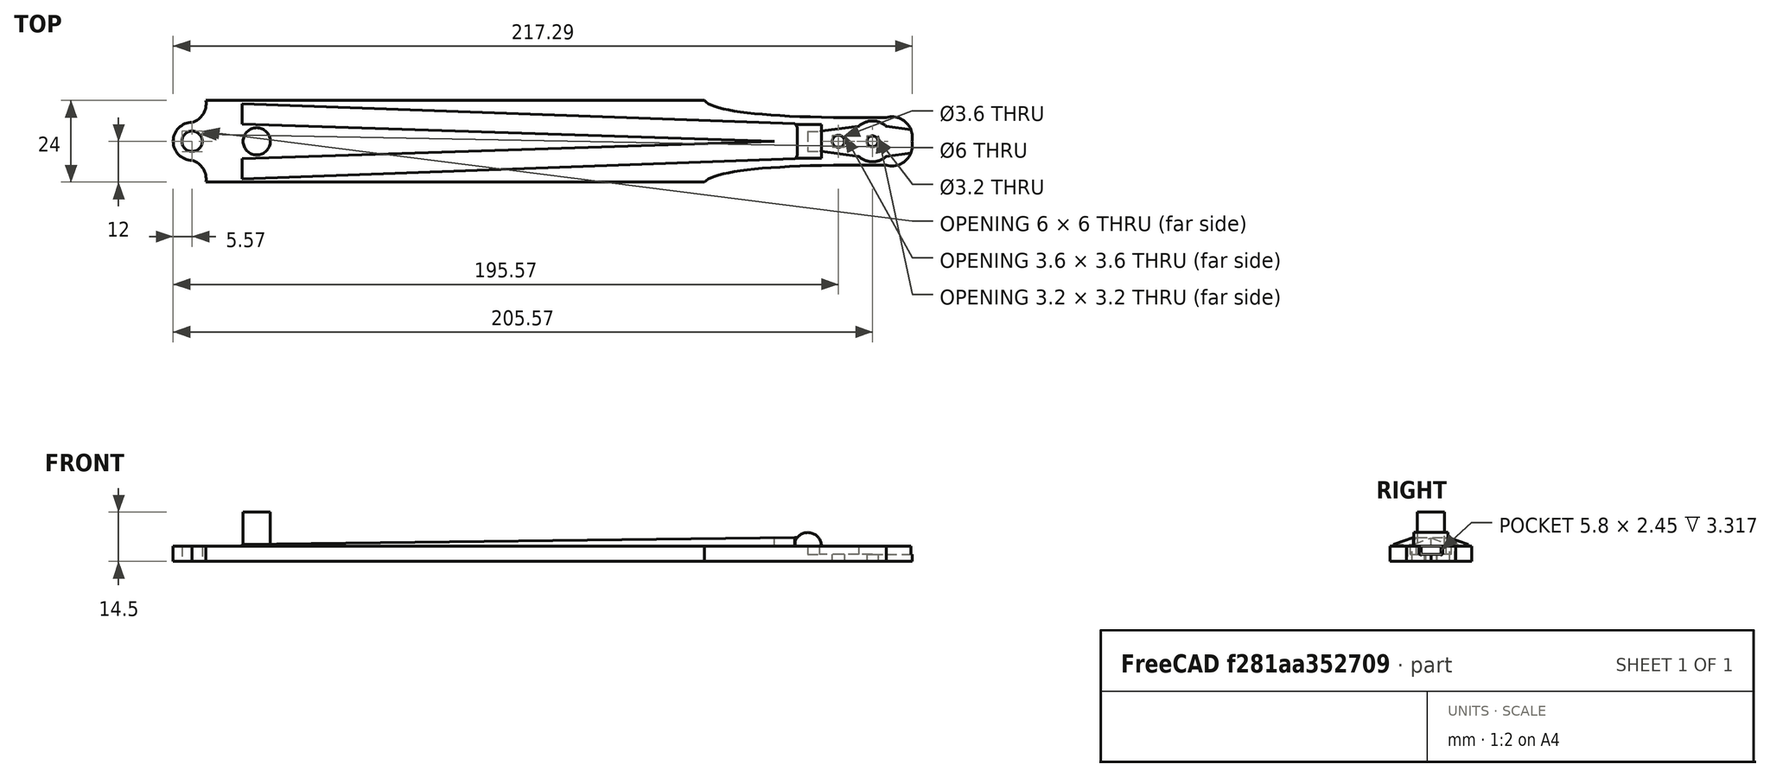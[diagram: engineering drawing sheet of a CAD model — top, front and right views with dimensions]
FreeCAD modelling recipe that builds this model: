
FCSTD DOCUMENT  (FreeCAD 0.18.4R)
Label: Servo_reset_Arm
License: All rights reserved
LicenseURL: http://en.wikipedia.org/wiki/All_rights_reserved
objects: TechDraw::DrawViewDimension×10, Sketcher::SketchObject×8, TechDraw::DrawViewPart×5, Part::Extrusion×4, Part::Mirroring×2, Part::MultiFuse×2, Part::Cut×2, TechDraw::DrawSVGTemplate×2, TechDraw::DrawViewAnnotation×2, TechDraw::DrawPage×2, PartDesign::Pad×2, Spreadsheet::Sheet×1, Part::Fuse×1, PartDesign::FeatureBase×1, PartDesign::Pocket×1, PartDesign::Body×1, TechDraw::DrawProjGroupItem×1, TechDraw::DrawProjGroup×1
note: 27 computed .brp shape members not serialized (recipe doc carries the construction recipe); baked Part::Feature solids carry a one-line shape summary decoded from their .brp

FEATURE [Sketcher::SketchObject] Sketch001
  sketch-geometry (19):
    g0: GeomPoint X=-195.949 Y=12 Z=0
    g1: LineSegment StartX=-195.949 StartY=12 StartZ=0 EndX=-49.4478 EndY=12 EndZ=0
    g2: Circle [constr] CenterX=4.05129 CenterY=7 CenterZ=0 NormalX=0 NormalY=0 NormalZ=1 AngleXU=0 Radius=6
    g3: ArcOfCircle CenterX=5.68089 CenterY=1.18713 CenterZ=0 NormalX=0 NormalY=0 NormalZ=1 AngleXU=0 Radius=6.03698 StartAngle=6.08525 EndAngle=8.12731
    g4: ArcOfCircle CenterX=0 CenterY=0 CenterZ=0 NormalX=0 NormalY=0 NormalZ=1 AngleXU=0 Radius=1.6 StartAngle=0 EndAngle=3.14159
    g5: LineSegment StartX=1.6 StartY=0 StartZ=0 EndX=11.6 EndY=0 EndZ=0
    g6: LineSegment StartX=-1.6 StartY=0 StartZ=0 EndX=-90.499 EndY=0 EndZ=0
    g7: Circle [constr] CenterX=4.05129 CenterY=7 CenterZ=0 NormalX=0 NormalY=0 NormalZ=1 AngleXU=0 Radius=5
    g8: Circle [constr] CenterX=-44.341 CenterY=6.58855 CenterZ=0 NormalX=0 NormalY=0 NormalZ=1 AngleXU=0 Radius=5
    g9: Circle [constr] CenterX=-49.4478 CenterY=12 CenterZ=0 NormalX=0 NormalY=0 NormalZ=1 AngleXU=0 Radius=5
    g10: BSplineCurve PolesCount=3 KnotsCount=2 Degree=2 IsPeriodic=0
    g11: GeomPoint [constr] X=4.05129 Y=7 Z=0
    g12: GeomPoint [constr] X=-49.4478 Y=12 Z=0
    g13: ArcOfCircle CenterX=-201.618 CenterY=11.0828 CenterZ=0 NormalX=0 NormalY=0 NormalZ=1 AngleXU=0 Radius=5.74276 StartAngle=4.99796 EndAngle=6.44358
    g14: ArcOfCircle CenterX=-200 CenterY=0 CenterZ=0 NormalX=0 NormalY=0 NormalZ=1 AngleXU=0 Radius=5.57264 StartAngle=1.5708 EndAngle=3.14159
    g15: ArcOfCircle CenterX=-200 CenterY=0 CenterZ=0 NormalX=0 NormalY=0 NormalZ=1 AngleXU=0 Radius=3 StartAngle=0 EndAngle=3.14159
    g16: LineSegment StartX=-205.573 StartY=7e-16 StartZ=0 EndX=-203 EndY=0 EndZ=0
    g17: LineSegment StartX=-197 StartY=0 StartZ=0 EndX=-90.499 EndY=0 EndZ=0
    g18: LineSegment [constr] StartX=-200 StartY=5.57264 StartZ=0 EndX=-200 EndY=0 EndZ=0
  constraints (43):
    c: DistanceX(g0,g2) = 200  'length'
    c: DistanceY(g2,g0) = 5
    c: Coincident(g1,g0)
    c: Horizontal(g1)
    c: Radius(g2) = 6
    c: PointOnObject(g3,g-1)
    c: PointOnObject(g6,g-1)
    c: Coincident(g4,g-1)
    c: PointOnObject(g4,g-1)
    c: Coincident(g5,g4)
    c: Coincident(g5,g3)
    c: Horizontal(g5)
    c: Coincident(g6,g4)
    c: Radius(g4) = 1.6
    c: Radius(g7) = 5
    c: Equal(g7,g8)
    c: Equal(g7,g9)
    c: Coincident(g9,g1)
    c: InternalAlignment(g7,g10)
    c: InternalAlignment(g8,g10)
    c: InternalAlignment(g9,g10)
    c: InternalAlignment(g11,g10)
    c: InternalAlignment(g12,g10)
    c: Coincident(g7,g2)
    c: Coincident(g13,g0)
    c: Coincident(g14,g13)
    c: PointOnObject(g14,g-1)
    c: DistanceX(g5,g5) = 10
    c: Coincident(g3,g10)
    c: DistanceY(g6,g0) = 12
    c: Coincident(g15,g14)
    c: PointOnObject(g15,g-1)
    c: Coincident(g17,g6)
    c: Horizontal(g17)
    c: Coincident(g15,g17)
    c: Coincident(g16,g14)
    c: PointOnObject(g14,g-1)
    c: Coincident(g16,g15)
    c: Coincident(g18,g13)
    c: Coincident(g18,g14)
    c: Radius(g15) = 3
    c: DistanceX(g14,g4) = 200
    c: Vertical(g18)
FEATURE [Part::Extrusion] Extrude  label="arm"
  Base = -> Sketch001
  Dir = (0,0,1)
  DirMode = 2
  FaceMakerClass = Part::FaceMakerBullseye
  LengthFwd = 4.5
  LengthRev = 0
  Solid = true
  Symmetric = false
  expr: LengthFwd = global.height
FEATURE [Sketcher::SketchObject] Sketch008  label="servoHolderHole"
  AttachmentOffset = pos=(0,0,0) rot=(0,0,1;1.5708rad)
  MapMode = 5
  Placement = pos=(0,0,4.5) rot=(0,0,1;1.5708rad)
  Support = -> [Extrude]
  sketch-geometry (7):
    g0: GeomPoint X=0 Y=19 Z=0
    g1: LineSegment StartX=0 StartY=19 StartZ=0 EndX=2.9 EndY=19 EndZ=0
    g2: LineSegment StartX=2.9 StartY=19 StartZ=0 EndX=2.9 EndY=15.6827 EndZ=0
    g3: ArcOfCircle CenterX=0 CenterY=0 CenterZ=0 NormalX=0 NormalY=0 NormalZ=1 AngleXU=0 Radius=6 StartAngle=0 EndAngle=0.747584
    g4: LineSegment StartX=4.4 StartY=4.07922 StartZ=0 EndX=2.9 EndY=15.6827 EndZ=0
    g5: LineSegment StartX=0 StartY=0 StartZ=0 EndX=6 EndY=0 EndZ=0
    g6: LineSegment StartX=0 StartY=0 StartZ=0 EndX=0 EndY=19 EndZ=0
  constraints (18):
    c: PointOnObject(g0,g-2)
    c: DistanceY(g-1,g0) = 19  'servHoleL'
    c: Coincident(g1,g0)
    c: Horizontal(g1)
    c: DistanceX(g1,g1) = 2.9
    c: Coincident(g2,g1)
    c: Vertical(g2)
    c: Coincident(g3,g-1)
    c: Radius(g3) = 6
    c: PointOnObject(g3,g-1)
    c: DistanceX(g-1,g3) = 4.4
    c: Coincident(g4,g2)
    c: Distance(g4) = 11.7
    c: Coincident(g4,g3)
    c: Coincident(g5,g-1)
    c: Coincident(g5,g3)
    c: Coincident(g6,g-1)
    c: Coincident(g6,g0)
FEATURE [Spreadsheet::Sheet] Spreadsheet  label="global"
  cells = A1=height; B1(height)=4.5; A2=offsetBackwardServo; B2(offestSev)=-2.5
FEATURE [Part::Extrusion] Extrude004
  Base = -> Sketch008
  Dir = (0,0,1)
  DirMode = 2
  FaceMakerClass = Part::FaceMakerBullseye
  LengthFwd = 2.45
  LengthRev = 0
  Reversed = true
  Solid = true
  Symmetric = false
FEATURE [Part::Mirroring] Part__Mirroring002  label="Extrude004 (Mirror #3)"
  Base = (0,0,0)
  Normal = (1,0,0)
  Source = -> Extrude004
FEATURE [Part::MultiFuse] Fusion003
  Shapes = -> [Part__Mirroring002,Extrude004]
FEATURE [Part::Cut] Cut
  Base = -> Extrude
  Tool = -> Fusion003
FEATURE [Part::Mirroring] Part__Mirroring  label="Extrude (Mirror #1)"
  Base = (0,0,0)
  Normal = (0,1,0)
  Source = -> Cut
FEATURE [Sketcher::SketchObject] Sketch012
  MapMode = 5
  Placement = pos=(0,0,4) rot=(0,0,1;0rad)
  sketch-geometry (9):
    g0: LineSegment StartX=-185.355 StartY=11.0268 StartZ=0 EndX=-22.8408 EndY=5.14242 EndZ=0
    g1: LineSegment StartX=-22.8408 StartY=-5.14242 StartZ=0 EndX=-185.355 EndY=-11.0268 EndZ=0
    g2: LineSegment StartX=-185.355 StartY=-11.0268 StartZ=0 EndX=-185.355 EndY=-5.02676 EndZ=0
    g3: LineSegment StartX=-185.355 StartY=-5.02676 StartZ=0 EndX=-28.8408 EndY=0 EndZ=0
    g4: LineSegment StartX=-28.8408 StartY=0 StartZ=0 EndX=-185.355 EndY=5.02676 EndZ=0
    g5: LineSegment StartX=-185.355 StartY=5.02676 StartZ=0 EndX=-185.355 EndY=11.0268 EndZ=0
    g6: ArcOfCircle CenterX=-28.8408 CenterY=0 CenterZ=0 NormalX=0 NormalY=0 NormalZ=1 AngleXU=0 Radius=7.90218 StartAngle=5.5746 EndAngle=6.99177
    g7: LineSegment [constr] StartX=-185.355 StartY=5.02676 StartZ=0 EndX=-185.355 EndY=0 EndZ=0
    g8: LineSegment [constr] StartX=-185.355 StartY=0 StartZ=0 EndX=-185.355 EndY=-5.02676 EndZ=0
  constraints (22):
    c: Coincident(g2,g1)
    c: Vertical(g2)
    c: Coincident(g3,g2)
    c: PointOnObject(g3,g-1)
    c: Coincident(g4,g3)
    c: Coincident(g5,g4)
    c: Coincident(g5,g0)
    c: Vertical(g5)
    c: DistanceY(g2,g2) = 6
    c: DistanceY(g5,g5) = 6
    c: Coincident(g6,g3)
    c: Coincident(g6,g0)
    c: Coincident(g6,g1)
    c: DistanceX(g3,g0) = 6
    c: DistanceX(g3,g1) = 6
    c: Coincident(g7,g4)
    c: PointOnObject(g7,g-1)
    c: Coincident(g8,g7)
    c: Coincident(g8,g2)
    c: Vertical(g7)
    c: Vertical(g8)
    c: Equal(g7,g8)
FEATURE [Sketcher::SketchObject] Sketch013
  MapMode = 5
  Placement = pos=(0,0,0) rot=(1,0,0;1.5708rad)
  sketch-geometry (3):
    g0: LineSegment StartX=-190 StartY=5 StartZ=0 EndX=-22.1184 EndY=7 EndZ=0
    g1: LineSegment StartX=-22.1184 StartY=7 StartZ=0 EndX=-190 EndY=7 EndZ=0
    g2: LineSegment StartX=-190 StartY=7 StartZ=0 EndX=-190 EndY=5 EndZ=0
  constraints (8):
    c: Coincident(g1,g0)
    c: Horizontal(g1)
    c: Coincident(g2,g1)
    c: Coincident(g2,g0)
    c: Vertical(g2)
    c: DistanceX(g0,g-1) = 190
    c: DistanceY(g-1,g0) = 7
    c: DistanceY(g0,g1) = 2
FEATURE [Part::Extrusion] Extrude005
  Base = -> Sketch012
  Dir = (0,0,1)
  DirMode = 2
  FaceMakerClass = Part::FaceMakerBullseye
  LengthFwd = 3
  LengthRev = 0
  Solid = true
  Symmetric = false
FEATURE [Part::Extrusion] Extrude006
  Base = -> Sketch013
  Dir = (0,-1,2e-16)
  DirMode = 2
  FaceMakerClass = Part::FaceMakerBullseye
  LengthFwd = 30
  LengthRev = 30
  Solid = true
  Symmetric = false
FEATURE [Part::Cut] Cut001  label="Strebe"
  Base = -> Extrude005
  Tool = -> Extrude006
FEATURE [Part::Fuse] Fusion
  Base = -> Cut
  Tool = -> Part__Mirroring
FEATURE [TechDraw::DrawSVGTemplate] Template
  EditableTexts = Designed_by_Name=Johannes Löwe; Drawing_number=0.0.1; FC-Date=24/03/2019; FC-SC=-; FC-SH=1; FC-Title=S.L.A.R Leg; Subtitle=Middle Component; Weight=19.5 g
  Height = 210
  Orientation = 1
  Width = 297
FEATURE [TechDraw::DrawViewPart] View  label="Top"
  Caption = Top
  CoarseView = true
  Direction = (0,0,1)
  Focus = 100
  HardHidden = false
  IsoCount = 0
  IsoHidden = false
  IsoVisible = true
  LockPosition = false
  Perspective = false
  Rotation = 0
  ScaleType = 1
  SeamHidden = false
  SeamVisible = false
  SmoothHidden = false
  SmoothVisible = true
  X = 133.52
  Y = 56.71
FEATURE [TechDraw::DrawViewPart] View001  label="Front"
  Caption = Front
  CoarseView = true
  Direction = (0,1,0)
  Focus = 100
  HardHidden = false
  IsoCount = 0
  IsoHidden = false
  IsoVisible = false
  LockPosition = false
  Perspective = true
  Rotation = 0
  ScaleType = 0
  SeamHidden = false
  SeamVisible = false
  SmoothHidden = false
  SmoothVisible = false
  X = 216.314
  Y = 87.8478
FEATURE [TechDraw::DrawViewPart] View002  label="Perspective"
  Caption = The S.L.A.R. Leg
  CoarseView = true
  Direction = (-0.2,1,1)
  Focus = 200
  HardHidden = false
  IsoCount = 0
  IsoHidden = false
  IsoVisible = true
  LockPosition = false
  Perspective = false
  Rotation = 0
  Scale = 1.5
  ScaleType = 0
  SeamHidden = false
  SeamVisible = false
  SmoothHidden = true
  SmoothVisible = false
  X = 69.0301
  Y = 169.689
  expr: Direction.x = -0.2
FEATURE [TechDraw::DrawViewDimension] Dimension
  Arbitrary = false
  FormatSpec = %.2f
  LockPosition = false
  MeasureType = 1
  OverTolerance = 0
  References2D = -> [View]
  Rotation = 0
  ScaleType = 0
  Type = 2
  UnderTolerance = 0
  X = -113.183
  Y = -28.0041
FEATURE [TechDraw::DrawViewDimension] Dimension001
  Arbitrary = false
  FormatSpec = %.2f
  LockPosition = false
  MeasureType = 1
  OverTolerance = 0
  References2D = -> [View001]
  Rotation = 0
  ScaleType = 0
  Type = 1
  UnderTolerance = 0
  X = 31.1719
  Y = 20.5356
FEATURE [TechDraw::DrawViewDimension] Dimension002
  Arbitrary = false
  FormatSpec = %.2f
  LockPosition = false
  MeasureType = 1
  OverTolerance = 0
  References2D = -> [View]
  Rotation = 0
  ScaleType = 0
  Type = 2
  UnderTolerance = 0
  X = -69.0862
  Y = -0.822454
FEATURE [TechDraw::DrawViewDimension] Dimension003
  Arbitrary = false
  FormatSpec = %.2f
  LockPosition = false
  MeasureType = 1
  OverTolerance = 0
  References2D = -> [View]
  Rotation = 0
  ScaleType = 0
  Type = 2
  UnderTolerance = 0
  X = -91.294
  Y = -1.64851
FEATURE [TechDraw::DrawViewDimension] Dimension004
  Arbitrary = false
  FormatSpec = %.2f
  LockPosition = false
  MeasureType = 1
  OverTolerance = 0
  References2D = -> [View002]
  Rotation = 0
  ScaleType = 0
  Type = 0
  UnderTolerance = 0
  X = 1.50159
  Y = -39.0413
FEATURE [TechDraw::DrawViewAnnotation] Annotation
  Font = osifont
  LineSpace = 80
  LockPosition = false
  MaxWidth = -1
  Rotation = 0
  ScaleType = 0
  Text = Radboud University
  TextSize = 5
  TextStyle = 2
  X = 214.014
  Y = 35.8125
FEATURE [TechDraw::DrawPage] Page
  KeepUpdated = true
  ProjectionType = 0
  Template = -> Template
  Views = -> [View,View001,View002,Dimension,Dimension001,Dimension002,Dimension003,Dimension004,Annotation]
FEATURE [Part::MultiFuse] Fusion004
  Shapes = -> [Cut001,Fusion]
FEATURE [PartDesign::FeatureBase] BaseFeature
  BaseFeature = -> Fusion004
FEATURE [Sketcher::SketchObject] Sketch015  label="HoleServoScrew2"
  MapMode = 5
  Placement = pos=(0,0,4) rot=(0,0,1;0rad)
  sketch-geometry (1):
    g0: Circle CenterX=-10 CenterY=0 CenterZ=0 NormalX=0 NormalY=0 NormalZ=1 AngleXU=0 Radius=1.8
  constraints (3):
    c: PointOnObject(g0,g-1)
    c: DistanceX(g0,g-1) = 10
    c: Radius(g0) = 1.8
FEATURE [Sketcher::SketchObject] Sketch  label="shoe"
  Placement = pos=(0,0,0) rot=(1,0,0;1.5708rad)
  expr: Constraints[4] = arm.LengthFwd
  expr: Constraints[6] = servoHolderHole.Constraints.servHoleL
  sketch-geometry (2):
    g0: ArcOfCircle CenterX=-19 CenterY=4.5 CenterZ=0 NormalX=0 NormalY=0 NormalZ=1 AngleXU=0 Radius=4 StartAngle=0 EndAngle=3.14159
    g1: LineSegment StartX=-23 StartY=4.5 StartZ=0 EndX=-15 EndY=4.5 EndZ=0
  constraints (7):
    c: Radius(g0) = 4
    c: Coincident(g1,g0)
    c: Coincident(g1,g0)
    c: Horizontal(g1)
    c: DistanceY(g-1,g0) = 4.5
    c: PointOnObject(g0,g1)
    c: DistanceX(g0,g-1) = 19
FEATURE [PartDesign::Pad] Pad
  BaseFeature = -> BaseFeature
  Length = 5
  Length2 = 5
  Profile = -> Sketch
  Reversed = true
  Type = 4
FEATURE [PartDesign::Pocket] Pocket
  BaseFeature = -> Pad
  Length = 28
  Length2 = 100
  Midplane = true
  Profile = -> Sketch015
  Type = 0
FEATURE [Sketcher::SketchObject] Sketch016
  MapMode = 45
  Placement = pos=(-113.608,6.1e-15,4.5) rot=(0,0,1;1.5708rad)
  Support = -> [Pocket]
FEATURE [Sketcher::SketchObject] Sketch017  label="pole"
  MapMode = 45
  Placement = pos=(-113.608,6.1e-15,4.5) rot=(0,0,1;1.5708rad)
  Support = -> [Pocket]
  sketch-geometry (1):
    g0: Circle CenterX=0 CenterY=67.4065 CenterZ=0 NormalX=0 NormalY=0 NormalZ=1 AngleXU=0 Radius=4
  constraints (2):
    c: PointOnObject(g0,g-2)
    c: Radius(g0) = 4
FEATURE [PartDesign::Pad] Pad001
  BaseFeature = -> Pocket
  Length = 10
  Length2 = 100
  Profile = -> Sketch017
  Refine = true
  Type = 0
FEATURE [PartDesign::Body] Body
  BaseFeature = -> Fusion004
  Group = -> [BaseFeature,Sketch015,Sketch,Pad,Pocket,Sketch017,Pad001]
  Origin = -> Origin
  Tip = -> Pad001
FEATURE [TechDraw::DrawSVGTemplate] Template001
  EditableTexts = Designed_by_Name=Johannes Loewe; Drawing_number=0.0.1; FC-Date=08/08/2021; FC-SC=1; FC-SH=1; FC-Title=RWML Crawler; Subtitle=Reset Leg; Weight=20g
  Height = 210
  Orientation = 1
  Width = 297
FEATURE [TechDraw::DrawViewPart] View003  label=" Perspective"
  CoarseView = false
  Direction = (-0.035,-0.289,0.957)
  Focus = 100
  HardHidden = false
  IsoCount = 0
  IsoHidden = false
  IsoVisible = false
  LockPosition = false
  Perspective = false
  Rotation = 0
  ScaleType = 0
  SeamHidden = false
  SeamVisible = false
  SmoothHidden = false
  SmoothVisible = true
  Source = -> [Body]
  X = 175.744
  Y = 171.55
FEATURE [TechDraw::DrawProjGroupItem] ProjItem  label=" Front"
  CoarseView = false
  Direction = (0,-0.95,0)
  Focus = 100
  HardHidden = false
  IsoCount = 0
  IsoHidden = false
  IsoVisible = false
  LockPosition = true
  Perspective = false
  Rotation = 0
  RotationVector = (90,0,0)
  ScaleType = 2
  SeamHidden = false
  SeamVisible = false
  SmoothHidden = false
  SmoothVisible = false
  Source = -> [Body]
  Type = 0
  X = 0
  Y = 0
FEATURE [TechDraw::DrawProjGroup] ProjGroup
  Anchor = -> ProjItem
  AutoDistribute = true
  LockPosition = false
  ProjectionType = 0
  Rotation = 0
  ScaleType = 0
  Source = -> [Body]
  Views = -> [ProjItem]
  X = 174.074
  Y = 95.6648
  spacingX = 15
  spacingY = 15
FEATURE [TechDraw::DrawViewPart] View004  label=" Top"
  CoarseView = false
  Direction = (0,0,1)
  Focus = 100
  HardHidden = false
  IsoCount = 0
  IsoHidden = false
  IsoVisible = false
  LockPosition = false
  Perspective = false
  Rotation = 90
  Scale = 0.8
  ScaleType = 0
  SeamHidden = false
  SeamVisible = false
  SmoothHidden = false
  SmoothVisible = false
  Source = -> [Body]
  X = 30.3466
  Y = 105.658
FEATURE [TechDraw::DrawViewDimension] Dimension005
  Arbitrary = false
  FormatSpec = %.2f
  LockPosition = false
  MeasureType = 1
  OverTolerance = 0
  References2D = -> [ProjItem]
  Rotation = 0
  ScaleType = 0
  Type = 1
  UnderTolerance = 0
  X = -26.9748
  Y = -14.0567
FEATURE [TechDraw::DrawViewDimension] Dimension006
  Arbitrary = false
  FormatSpec = %.2f
  LockPosition = false
  MeasureType = 1
  OverTolerance = 0
  References2D = -> [ProjItem]
  Rotation = 0
  ScaleType = 0
  Type = 2
  UnderTolerance = 0
  X = 94.4241
  Y = 5.08403
FEATURE [TechDraw::DrawViewDimension] Dimension007
  Arbitrary = false
  FormatSpec = %.2f
  LockPosition = false
  MeasureType = 1
  OverTolerance = 0
  References2D = -> [ProjItem]
  Rotation = 0
  ScaleType = 0
  Type = 2
  UnderTolerance = 0
  X = -74.5413
  Y = 14.174
FEATURE [TechDraw::DrawViewDimension] Dimension008
  Arbitrary = false
  FormatSpec = ⌀%.2f
  LockPosition = false
  MeasureType = 1
  OverTolerance = 0
  References2D = -> [View004]
  Rotation = 0
  ScaleType = 0
  Type = 5
  UnderTolerance = 0
  X = 18.9199
  Y = 73.7861
FEATURE [TechDraw::DrawViewDimension] Dimension009
  Arbitrary = false
  FormatSpec = ⌀%.2f
  LockPosition = false
  MeasureType = 1
  OverTolerance = 0
  References2D = -> [View004]
  Rotation = 0
  ScaleType = 0
  Type = 5
  UnderTolerance = 0
  X = 19.0993
  Y = 57.0201
FEATURE [TechDraw::DrawViewAnnotation] Annotation001
  Font = DejaVu Sans
  LineSpace = 80
  LockPosition = false
  MaxWidth = -1
  Rotation = 0
  ScaleType = 0
  Text = NUI Galway
  TextSize = 6
  TextStyle = 2
  X = 209.486
  Y = 34.5785
FEATURE [TechDraw::DrawPage] Page001
  KeepUpdated = true
  ProjectionType = 0
  Template = -> Template001
  Views = -> [View003,ProjGroup,View004,Dimension005,Dimension006,Dimension007,Dimension008,Dimension009,Annotation001]
